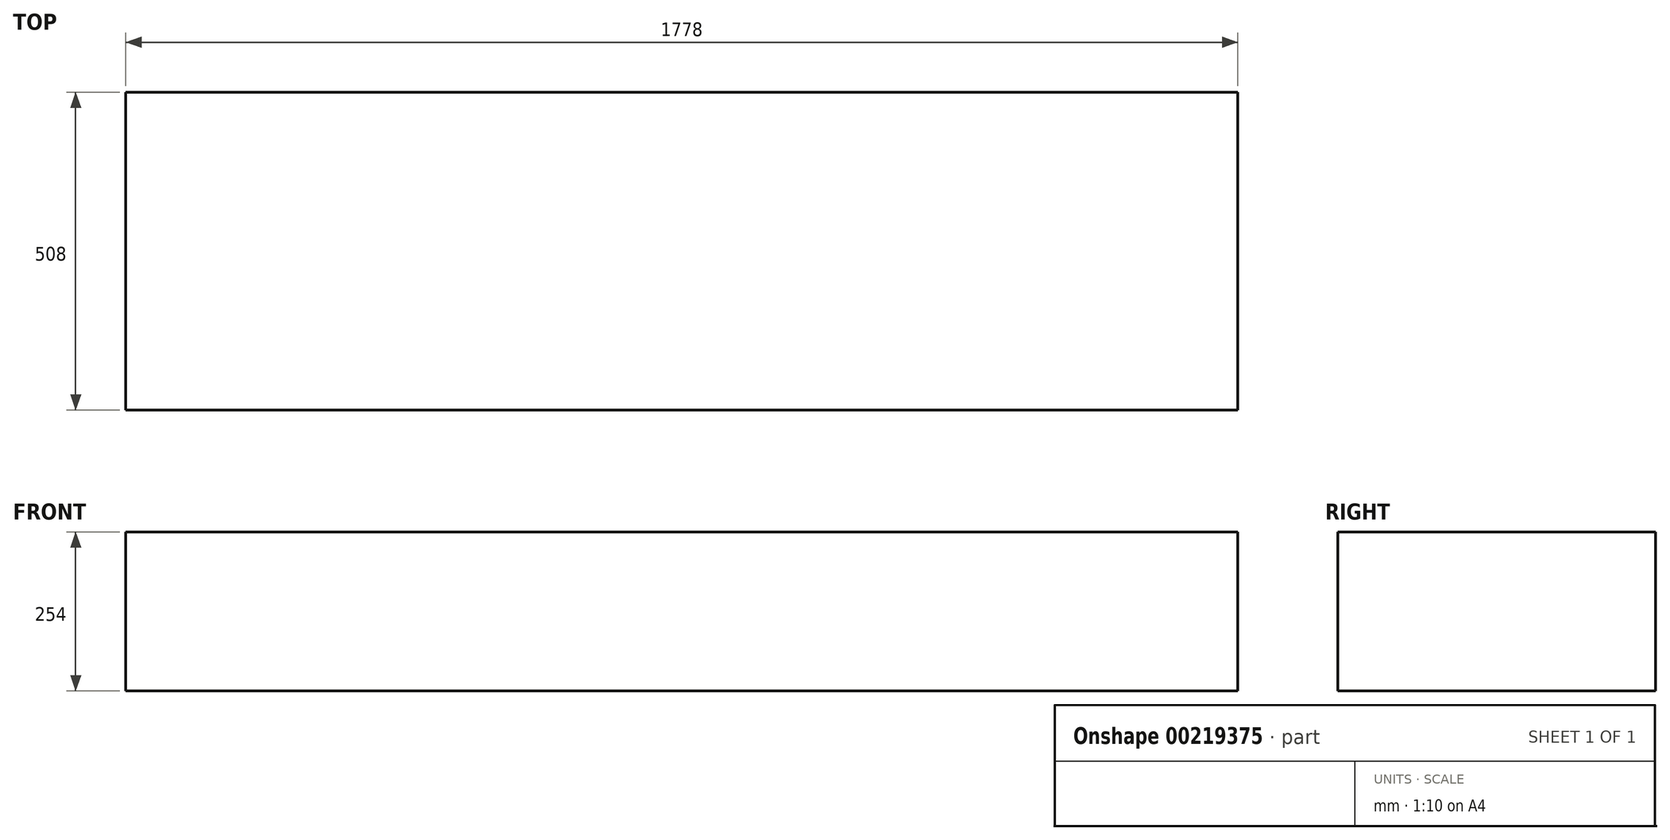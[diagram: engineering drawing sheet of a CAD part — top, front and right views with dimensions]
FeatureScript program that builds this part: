
annotation { "Feature Type Name" : "Feature", "Feature Type Description" : "" }
export const myFeature = defineFeature(function(context is Context, id is Id, definition is map)
    precondition{}
    {
        {
            var Q0;
            Q0=qCreatedBy(makeId("Front.planeOp"),FACE);
            var sketch = newSketch(context, id + "F0", { "sketchPlane" : qUnion([Q0])});
            skLineSegment(sketch, "E0.bottom", {"start": v(889, -127) * mm, "end": v(-889, -127) * mm});
            skLineSegment(sketch, "E0.top", {"start": v(889, 127) * mm, "end": v(-889, 127) * mm});
            skLineSegment(sketch, "E0.left", {"start": v(889, -127) * mm, "end": v(889, 127) * mm});
            skLineSegment(sketch, "E0.right", {"start": v(-889, -127) * mm, "end": v(-889, 127) * mm});
            skPoint(sketch, "E0.middle", {"position": v(0, 0) * mm});
            skLineSegment(sketch, "E1.bottom", {"start": v(-889, -127) * mm, "end": v(-584.2, -127) * mm});
            skLineSegment(sketch, "E1.top", {"start": v(-889, -736.6) * mm, "end": v(-584.2, -736.6) * mm});
            skLineSegment(sketch, "E1.left", {"start": v(-889, -127) * mm, "end": v(-889, -736.6) * mm});
            skLineSegment(sketch, "E1.right", {"start": v(-584.2, -127) * mm, "end": v(-584.2, -736.6) * mm});
            skLineSegment(sketch, "E2.bottom", {"start": v(889, -127) * mm, "end": v(584.2, -127) * mm});
            skLineSegment(sketch, "E2.top", {"start": v(889, -736.6) * mm, "end": v(584.2, -736.6) * mm});
            skLineSegment(sketch, "E2.left", {"start": v(889, -127) * mm, "end": v(889, -736.6) * mm});
            skLineSegment(sketch, "E2.right", {"start": v(584.2, -127) * mm, "end": v(584.2, -736.6) * mm});
            skSolve(sketch);
        }
        {
            var Q0;
            Q0=makeQuery(id+"F0.imprint","IMPRINT",FACE,{"disambiguationData":[TD([[makeQuery(id+"F0.imprint","IMPRINT",EDGE,{"derivedFrom":sQuery(id+"F0.wireOp",EDGE,"E0.bottom")}),-1.0]])]});
            var Q1;
            Q1=makeQuery(id+"F0.imprint","IMPRINT",FACE,{"disambiguationData":[TD([[makeQuery(id+"F0.imprint","IMPRINT",EDGE,{"derivedFrom":sQuery(id+"F0.wireOp",EDGE,"E1.bottom")}),-1.0]])]});
            var Q2;
            Q2=makeQuery(id+"F0.imprint","IMPRINT",FACE,{"disambiguationData":[TD([[makeQuery(id+"F0.imprint","IMPRINT",EDGE,{"derivedFrom":sQuery(id+"F0.wireOp",EDGE,"E2.bottom")}),1.0]])]});
            extrude(context, id + "F1", {"entities" : qUnion([Q0, Q1, Q2]), "depth" : 508 * mm});
        }
    });
